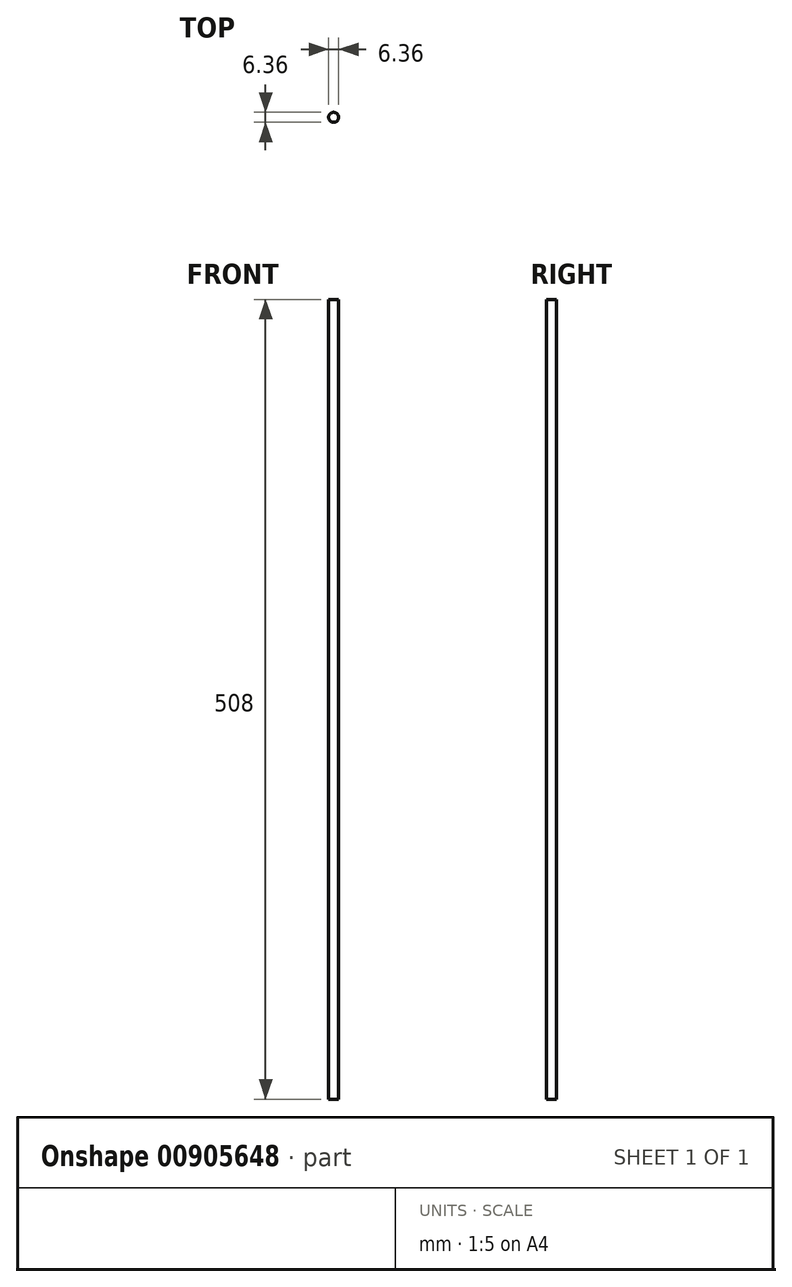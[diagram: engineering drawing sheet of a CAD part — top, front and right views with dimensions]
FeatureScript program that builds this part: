
annotation { "Feature Type Name" : "Feature", "Feature Type Description" : "" }
export const myFeature = defineFeature(function(context is Context, id is Id, definition is map)
    precondition{}
    {
        {
            var Q0;
            Q0=qCreatedBy(makeId("Top.planeOp"),FACE);
            var sketch = newSketch(context, id + "F0", { "sketchPlane" : qUnion([Q0])});
            skCircle(sketch, "E0", {"center": v(0, 0) * mm, "radius": 3.18 * mm});
            skSolve(sketch);
        }
        {
            var Q0;
            Q0 = qSketchRegion(id + "F0", true);
            extrude(context, id + "F1", {"entities" : qUnion([Q0]), "depth" : 508 * mm, "offsetDistance" : 25.4 * mm});
        }
    });
